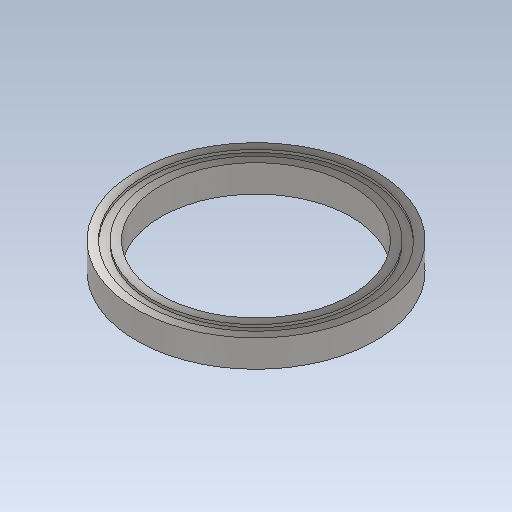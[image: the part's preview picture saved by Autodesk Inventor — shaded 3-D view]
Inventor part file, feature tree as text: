
AUTODESK INVENTOR PART (.ipt)
format: ipt  version: 2020 (Build 240168000, 168)  size: 146,944 bytes
history: native  units: mm
features: extrude x3, sketch x3, projected_geometry x1
ambient origin geometry x8: Origin, YZ Plane, XZ Plane, XY Plane, X Axis, Y Axis, Z Axis, Center Point
bodies: Solid1 (feature_tree)
feature tree (7):
  extrude  "Extrusion1"  Depth=44.0mm
  extrude  "Extrusion2"  Depth=5.0mm
  extrude  "Extrusion3"  Depth=0.5mm TaperAngle=0.0deg
  sketch  "Sketch1"  dims[d0=35.0mm d1=44.0mm]
  sketch  "Sketch2"  dims[d2=5.0mm d3=0.0mm d4=38.0mm]
  projected_geometry  "Projected Loop1"
  sketch  "Sketch3"  dims[d5=41.0mm d6=0.5mm d7=0.0mm d8=0.5mm d9=0.0mm]
